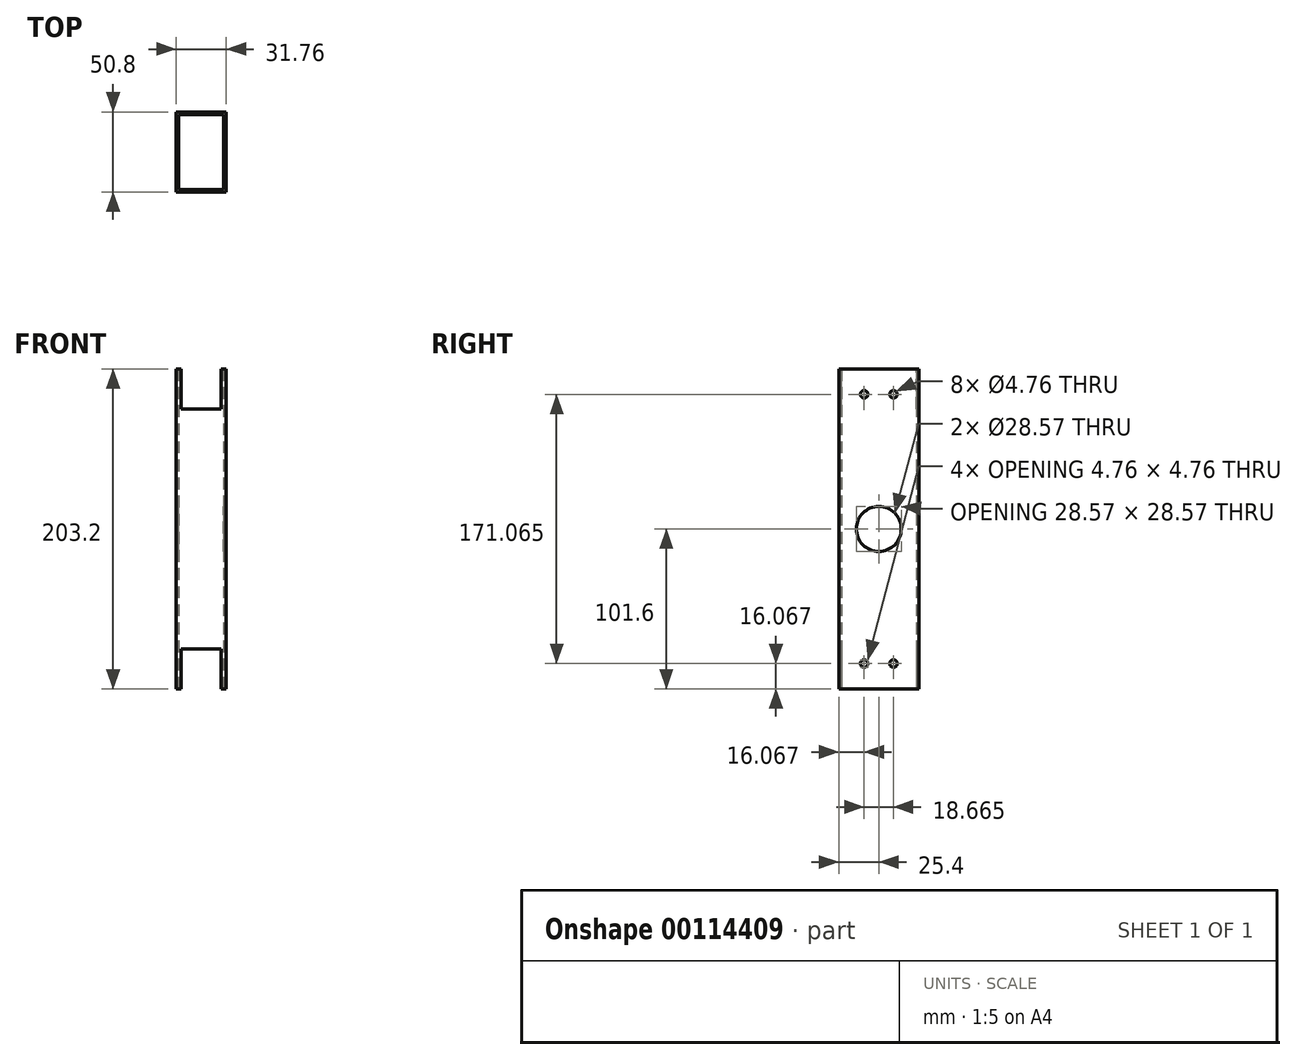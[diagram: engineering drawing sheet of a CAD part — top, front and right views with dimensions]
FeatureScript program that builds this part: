
annotation { "Feature Type Name" : "Feature", "Feature Type Description" : "" }
export const myFeature = defineFeature(function(context is Context, id is Id, definition is map)
    precondition{}
    {
        {
            var Q0;
            Q0=qCreatedBy(makeId("Top.planeOp"),FACE);
            var sketch = newSketch(context, id + "F0", { "sketchPlane" : qUnion([Q0])});
            skLineSegment(sketch, "E0.bottom", {"start": v(15.88, -25.4) * mm, "end": v(-15.87, -25.4) * mm});
            skLineSegment(sketch, "E0.top", {"start": v(15.88, 25.4) * mm, "end": v(-15.87, 25.4) * mm});
            skLineSegment(sketch, "E0.left", {"start": v(15.88, -25.4) * mm, "end": v(15.88, 25.4) * mm});
            skLineSegment(sketch, "E0.right", {"start": v(-15.87, -25.4) * mm, "end": v(-15.87, 25.4) * mm});
            skPoint(sketch, "E0.middle", {"position": v(0, 0) * mm});
            skLineSegment(sketch, "E1.bottom", {"start": v(14.3, 23.83) * mm, "end": v(-14.3, 23.83) * mm});
            skLineSegment(sketch, "E1.top", {"start": v(14.3, -23.83) * mm, "end": v(-14.3, -23.83) * mm});
            skLineSegment(sketch, "E1.left", {"start": v(14.3, 23.83) * mm, "end": v(14.3, -23.83) * mm});
            skLineSegment(sketch, "E1.right", {"start": v(-14.3, 23.83) * mm, "end": v(-14.3, -23.83) * mm});
            skSolve(sketch);
        }
        {
            var Q0;
            Q0=makeQuery(id+"F0.imprint","IMPRINT",FACE,{"disambiguationData":[TD([[makeQuery(id+"F0.imprint","IMPRINT",EDGE,{"derivedFrom":sQuery(id+"F0.wireOp",EDGE,"E0.bottom")}),-1.0]])]});
            extrude(context, id + "F1", {"entities" : qUnion([Q0]), "depth" : 101.6 * mm});
        }
        {
            var Q0;
            Q0=makeQuery(id+"F1.opExtrude","SWEPT_FACE",FACE,{"disambiguationData":[OSD([sQuery(id+"F0.wireOp",EDGE,"E0.bottom")])]});
            var sketch = newSketch(context, id + "F2", { "sketchPlane" : qUnion([Q0])});
            skLineSegment(sketch, "E2.bottom", {"start": v(12.7, 76.2) * mm, "end": v(-12.7, 76.2) * mm});
            skLineSegment(sketch, "E2.top", {"start": v(12.7, 127) * mm, "end": v(-12.7, 127) * mm});
            skLineSegment(sketch, "E2.left", {"start": v(12.7, 76.2) * mm, "end": v(12.7, 127) * mm});
            skLineSegment(sketch, "E2.right", {"start": v(-12.7, 76.2) * mm, "end": v(-12.7, 127) * mm});
            skPoint(sketch, "E2.middle", {"position": v(0, 101.6) * mm});
            skSolve(sketch);
        }
        {
            var Q0;
            {var subQ0=sQuery(id+"F2.wireOp",EDGE,"E2.bottom");Q0=makeQuery(id+"F2.imprint","IMPRINT",FACE,{"disambiguationData":[TD([[makeQuery(id+"F2.imprint","IMPRINT",EDGE,{"derivedFrom":subQ0}),-1.0]])]});}
            extrude(context, id + "F3", {"entities" : qUnion([Q0]), "operationType" : NewBodyOperationType.REMOVE, "endBound" : BoundingType.THROUGH_ALL, "oppositeDirection" : true, "depth" : 25.4 * mm});
        }
        {
            var Q0;
            Q0=makeQuery(id+"F1.opExtrude","SWEPT_FACE",FACE,{"disambiguationData":[OSD([sQuery(id+"F0.wireOp",EDGE,"E0.right")])]});
            var sketch = newSketch(context, id + "F4", { "sketchPlane" : qUnion([Q0])});
            skCircle(sketch, "E3", {"center": v(-9.33, 85.53) * mm, "radius": 2.38 * mm});
            skCircle(sketch, "E4.MirrorC", {"center": v(9.33, 85.53) * mm, "radius": 2.38 * mm});
            skSolve(sketch);
        }
        {
            var Q0;
            Q0 = qSketchRegion(id + "F4", true);
            extrude(context, id + "F5", {"entities" : qUnion([Q0]), "operationType" : NewBodyOperationType.REMOVE, "endBound" : BoundingType.THROUGH_ALL, "oppositeDirection" : true, "depth" : 25.4 * mm});
        }
        {
            var Q0;
            Q0=makeQuery(id+"F1.opExtrude","SWEPT_BODY",BODY,{"disambiguationData":[OSD([sQuery(id+"F0.wireOp",EDGE,"E0.bottom"),sQuery(id+"F0.wireOp",EDGE,"E0.top"),sQuery(id+"F0.wireOp",EDGE,"E0.left"),sQuery(id+"F0.wireOp",EDGE,"E0.right"),sQuery(id+"F0.wireOp",EDGE,"E1.bottom"),sQuery(id+"F0.wireOp",EDGE,"E1.top"),sQuery(id+"F0.wireOp",EDGE,"E1.left"),sQuery(id+"F0.wireOp",EDGE,"E1.right")])]});
            var Q1;
            Q1=qCreatedBy(makeId("Top.planeOp"),FACE);
            mirror(context, id + "F6", {"operationType" : NewBodyOperationType.ADD, "entities" : qUnion([Q0]), "mirrorPlane" : qUnion([Q1])});
        }
        {
            var Q0;
            {var subQ0=makeQuery(id+"F1.opExtrude","SWEPT_FACE",FACE,{"disambiguationData":[OSD([sQuery(id+"F0.wireOp",EDGE,"E0.right")])]});Q0=makeQuery(id+"F6.boolean.opBoolean","MERGE",FACE,{"derivedFrom":[subQ0,makeQuery(id+"F6.opPattern","COPY",FACE,{"derivedFrom":subQ0,"instanceName":"1"})]});}
            var sketch = newSketch(context, id + "F7", { "sketchPlane" : qUnion([Q0])});
            skCircle(sketch, "E5", {"center": v(0, 0) * mm, "radius": 14.29 * mm});
            skSolve(sketch);
        }
        {
            var Q0;
            Q0=makeQuery(id+"F7.imprint","IMPRINT",FACE,{"disambiguationData":[TD([[makeQuery(id+"F7.imprint","IMPRINT",EDGE,{"derivedFrom":sQuery(id+"F7.wireOp",EDGE,"E5")}),1.0]])]});
            extrude(context, id + "F8", {"entities" : qUnion([Q0]), "operationType" : NewBodyOperationType.REMOVE, "endBound" : BoundingType.THROUGH_ALL, "oppositeDirection" : true, "depth" : 25.4 * mm});
        }
    });
